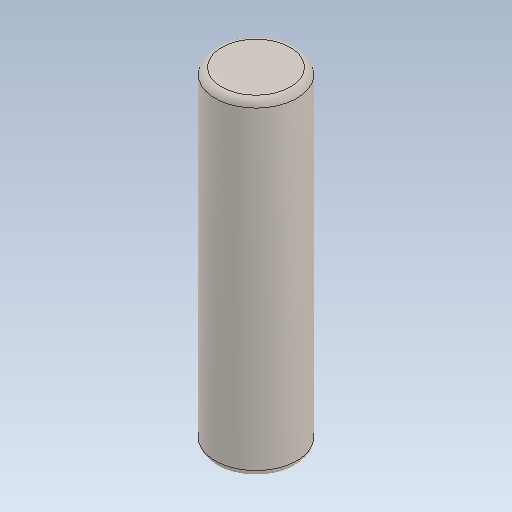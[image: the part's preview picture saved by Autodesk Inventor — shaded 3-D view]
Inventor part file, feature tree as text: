
AUTODESK INVENTOR PART (.ipt)
format: ipt  version: 2020.2 (Build 242310000, 310)  size: 95,232 bytes
history: native  units: in
note: dims shown in document units (in); Inventor stores cm internally (conversion verified against a paired STEP export)
features: revolve x1
ambient origin geometry x8: Origin, YZ Plane, XZ Plane, XY Plane, X Axis, Y Axis, Z Axis, Center Point
bodies: Solid1 (feature_tree)
feature tree (1):
  revolve  "Revolve1"  [1 undecoded]
note: 1 required parameter value undecoded (feature->parameter linkage not recoverable at this tier; creation-order binding heuristic only, values carry confidence <= 0.55)
